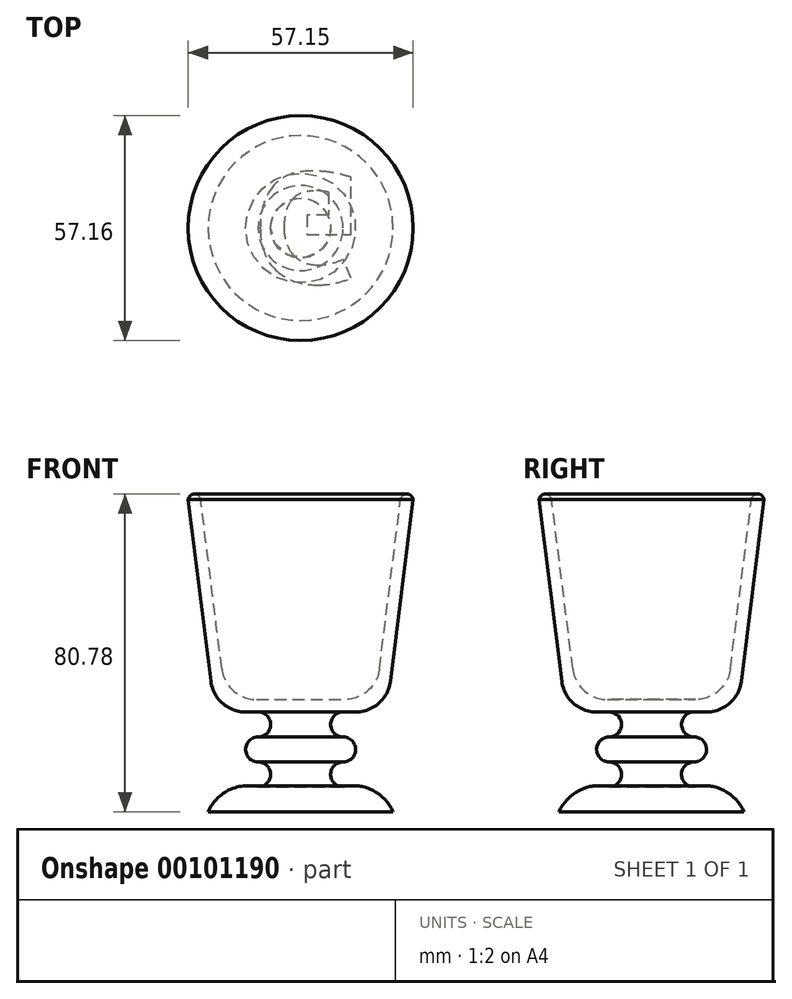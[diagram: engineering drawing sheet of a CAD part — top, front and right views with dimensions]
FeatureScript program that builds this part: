
annotation { "Feature Type Name" : "Feature", "Feature Type Description" : "" }
export const myFeature = defineFeature(function(context is Context, id is Id, definition is map)
    precondition{}
    {
        {
            var Q0;
            Q0=qCreatedBy(makeId("Front.planeOp"),FACE);
            var sketch = newSketch(context, id + "F0", { "sketchPlane" : qUnion([Q0])});
            skLineSegment(sketch, "E0", {"start": v(-10.55, -18.37) * mm, "end": v(-15.92, 24.64) * mm});
            skLineSegment(sketch, "E1", {"start": v(-19.1, 24.64) * mm, "end": v(-13.32, -21.55) * mm});
            skLineSegment(sketch, "E2", {"start": v(-4.5, -29.34) * mm, "end": v(-1.32, -29.34) * mm});
            skArc(sketch, "E3", {"start": v(-1.32, -35.69) * mm, "mid": v(1.86, -32.51) * mm, "end": v(-1.32, -29.34) * mm});
            skArc(sketch, "E4", {"start": v(-1.32, -35.69) * mm, "mid": v(-4.5, -38.86) * mm, "end": v(-1.32, -42.04) * mm});
            skLineSegment(sketch, "E5", {"start": v(-1.72, -26.16) * mm, "end": v(9.48, -26.16) * mm});
            skArc(sketch, "E6", {"start": v(-1.32, -48.39) * mm, "mid": v(1.87, -45.21) * mm, "end": v(-1.32, -42.04) * mm});
            skArc(sketch, "E7", {"start": v(-1.32, -48.39) * mm, "mid": v(-8.84, -49.22) * mm, "end": v(-14.02, -54.74) * mm});
            skPoint(sketch, "E8.visualSharp", {"position": v(-9.57, -26.16) * mm});
            skArc(sketch, "E8.filletArc", {"start": v(-10.55, -18.37) * mm, "mid": v(-7.6, -23.94) * mm, "end": v(-1.72, -26.16) * mm});
            skPoint(sketch, "E9.visualSharp", {"position": v(-12.35, -29.34) * mm});
            skArc(sketch, "E9.filletArc", {"start": v(-13.32, -21.55) * mm, "mid": v(-10.39, -27.11) * mm, "end": v(-4.5, -29.34) * mm});
            skArc(sketch, "E10", {"start": v(-15.92, 24.64) * mm, "mid": v(-17.5, 26.04) * mm, "end": v(-19.1, 24.64) * mm});
            skLineSegment(sketch, "E11", {"start": v(9.48, -54.74) * mm, "end": v(-14.02, -54.74) * mm});
            skLineSegment(sketch, "E12", {"start": v(9.48, -26.16) * mm, "end": v(9.48, -54.74) * mm});
            skLineSegment(sketch, "E13", {"start": v(9.48, -26.16) * mm, "end": v(9.48, 6.73) * mm, "construction": true});
            skSolve(sketch);
        }
        {
            var Q0;
            Q0=makeQuery(id+"F0.imprint","IMPRINT",FACE,{"disambiguationData":[TD([[makeQuery(id+"F0.imprint","IMPRINT",EDGE,{"derivedFrom":sQuery(id+"F0.wireOp",EDGE,"E0")}),1.0]])]});
            var Q1;
            Q1=sQuery(id+"F0.wireOp",EDGE,"E13");
            revolve(context, id + "F1", {"entities" : qUnion([Q0]), "axis" : qUnion([Q1]), "revolveType" : RevolveType.FULL});
        }
        {
            var Q0;
            Q0=makeQuery(id+"F1.opRevolve","SWEPT_FACE",FACE,{"disambiguationData":[OSD([sQuery(id+"F0.wireOp",EDGE,"E11")])]});
            var sketch = newSketch(context, id + "F2", { "sketchPlane" : qUnion([Q0])});
            skText(sketch, "E14", { "text": "G", "fontName": "OpenSans-Bold.ttf"});
            const initialGuessF2  = {"E14": [-0.00307, -0.0141, 1, 0, 0.0284]};
            skSetInitialGuess(sketch, initialGuessF2);
            skSolve(sketch);
        }
        {
            var Q0;
            Q0 = qSketchRegion(id + "F2", true);
            extrude(context, id + "F3", {"entities" : qUnion([Q0]), "operationType" : NewBodyOperationType.REMOVE, "oppositeDirection" : true, "depth" : 0.03 * mm});
        }
    });
